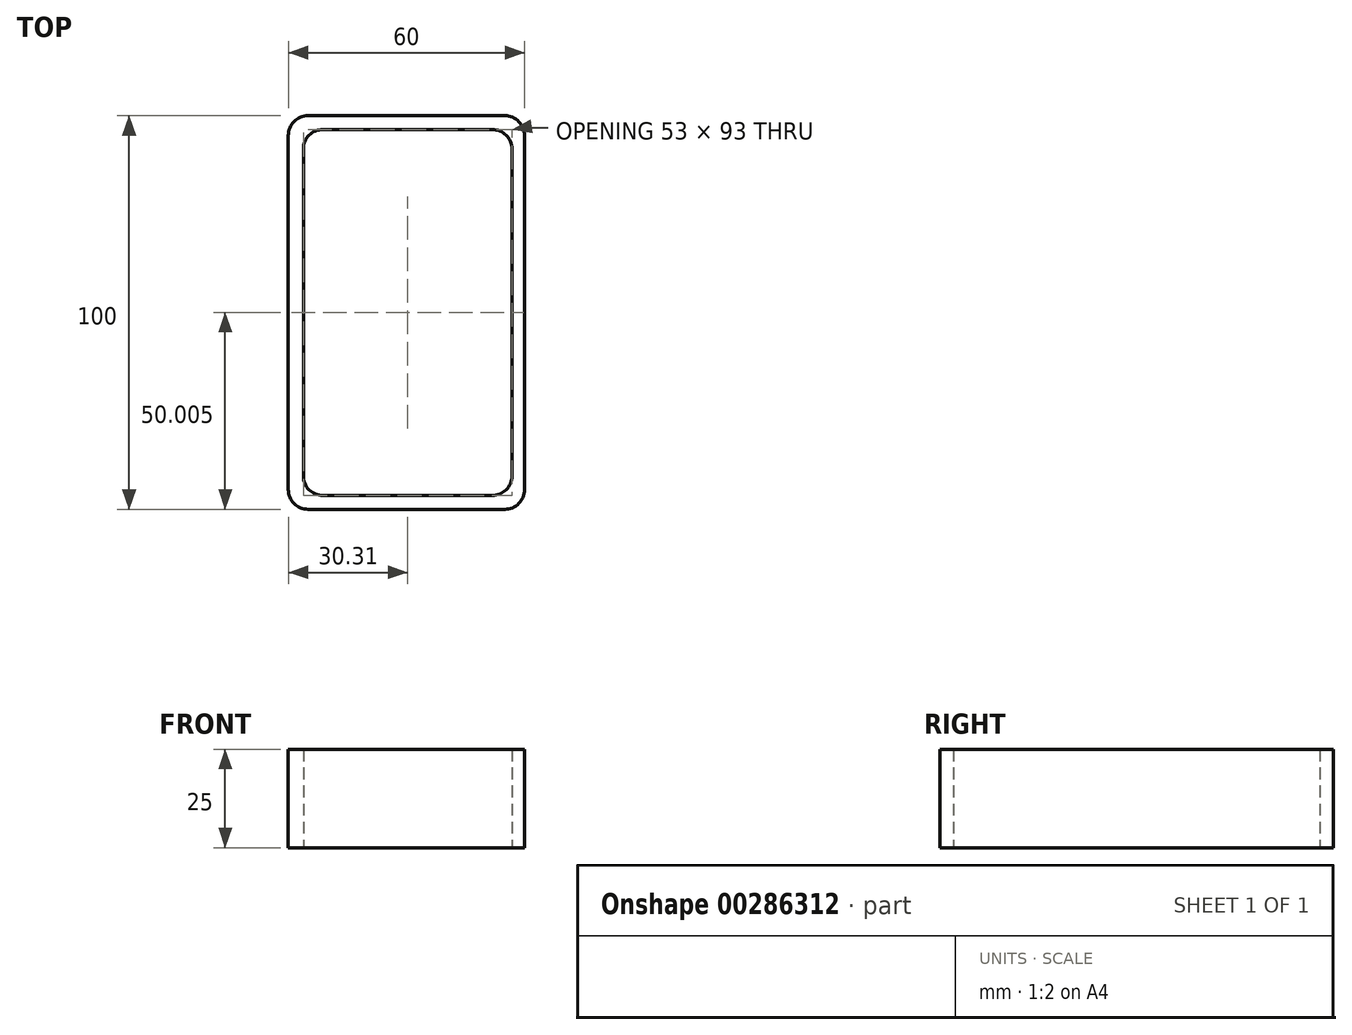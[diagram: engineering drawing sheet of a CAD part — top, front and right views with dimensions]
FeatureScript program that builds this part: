
annotation { "Feature Type Name" : "Feature", "Feature Type Description" : "" }
export const myFeature = defineFeature(function(context is Context, id is Id, definition is map)
    precondition{}
    {
        {
            var Q0;
            Q0=qCreatedBy(makeId("Top.planeOp"),FACE);
            var sketch = newSketch(context, id + "F0", { "sketchPlane" : qUnion([Q0])});
            skLineSegment(sketch, "E0", {"start": v(-48, 41.9) * mm, "end": v(-5, 41.9) * mm});
            skLineSegment(sketch, "E1", {"start": v(0, 36.9) * mm, "end": v(0, -46.1) * mm});
            skLineSegment(sketch, "E2", {"start": v(-53, 36.9) * mm, "end": v(-53, -46.1) * mm});
            skLineSegment(sketch, "E3", {"start": v(-48, -51.1) * mm, "end": v(-5, -51.1) * mm});
            skLineSegment(sketch, "E4", {"start": v(3.19, 40.4) * mm, "end": v(3.19, -49.6) * mm});
            skLineSegment(sketch, "E5", {"start": v(-1.81, -54.6) * mm, "end": v(-51.81, -54.6) * mm});
            skLineSegment(sketch, "E6", {"start": v(-56.81, 40.4) * mm, "end": v(-56.81, -49.6) * mm});
            skLineSegment(sketch, "E7", {"start": v(-51.81, 45.4) * mm, "end": v(-1.81, 45.4) * mm});
            skPoint(sketch, "E8.visualSharp", {"position": v(-53, 41.9) * mm});
            skArc(sketch, "E8.filletArc", {"start": v(-48, 41.9) * mm, "mid": v(-51.54, 40.43) * mm, "end": v(-53, 36.9) * mm});
            skPoint(sketch, "E9.visualSharp", {"position": v(-56.81, 45.4) * mm});
            skArc(sketch, "E9.filletArc", {"start": v(-51.81, 45.4) * mm, "mid": v(-55.35, 43.93) * mm, "end": v(-56.81, 40.4) * mm});
            skPoint(sketch, "E10.visualSharp", {"position": v(3.19, 45.4) * mm});
            skArc(sketch, "E10.filletArc", {"start": v(3.19, 40.4) * mm, "mid": v(1.72, 43.93) * mm, "end": v(-1.81, 45.4) * mm});
            skPoint(sketch, "E11.visualSharp", {"position": v(0, 41.9) * mm});
            skArc(sketch, "E11.filletArc", {"start": v(0, 36.9) * mm, "mid": v(-1.46, 40.43) * mm, "end": v(-5, 41.9) * mm});
            skPoint(sketch, "E12.visualSharp", {"position": v(3.19, -54.6) * mm});
            skArc(sketch, "E12.filletArc", {"start": v(-1.81, -54.6) * mm, "mid": v(1.72, -53.14) * mm, "end": v(3.19, -49.6) * mm});
            skPoint(sketch, "E13.visualSharp", {"position": v(0, -51.1) * mm});
            skArc(sketch, "E13.filletArc", {"start": v(-5, -51.1) * mm, "mid": v(-1.46, -49.64) * mm, "end": v(0, -46.1) * mm});
            skPoint(sketch, "E14.visualSharp", {"position": v(-53, -51.1) * mm});
            skArc(sketch, "E14.filletArc", {"start": v(-53, -46.1) * mm, "mid": v(-51.54, -49.64) * mm, "end": v(-48, -51.1) * mm});
            skPoint(sketch, "E15.visualSharp", {"position": v(-56.81, -54.6) * mm});
            skArc(sketch, "E15.filletArc", {"start": v(-56.81, -49.6) * mm, "mid": v(-55.35, -53.14) * mm, "end": v(-51.81, -54.6) * mm});
            skSolve(sketch);
        }
        {
            var Q0;
            Q0 = qSketchRegion(id + "F0", true);
            extrude(context, id + "F1", {"entities" : qUnion([Q0]), "depth" : 25 * mm});
        }
    });
